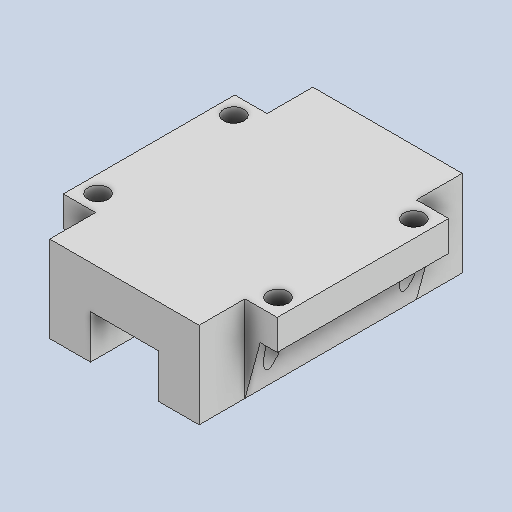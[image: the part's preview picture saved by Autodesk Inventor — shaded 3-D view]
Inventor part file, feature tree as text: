
AUTODESK INVENTOR PART (.ipt)
format: ipt  version: 2023 (Build 270158000, 158)  size: 184,832 bytes
history: native  units: mm
features: extrude x3, sketch x3
ambient origin geometry x8: Origin, YZ Plane, XZ Plane, XY Plane, X Axis, Y Axis, Z Axis, Center Point
bodies: Solid1 (feature_tree)
feature tree (6):
  extrude  "Extrusion1"  Depth=25.4mm
  extrude  "Extrusion2"  Depth=8.9mm
  extrude  "Extrusion3"  Depth=12.0mm
  sketch  "Sketch1"  dims[d0=63.0mm d1=25.4mm]
  sketch  "Sketch2"  dims[d4=21.5mm d5=8.9mm]
  sketch  "Sketch3"  dims[d6=12.9mm d7=12.0mm d8=5.0mm d9=50.5mm d10=0.0mm d11=13.5mm d12=64.0mm d13=0.0mm d14=0.0mm d15=6.0mm d16=40.0mm d17=53.0mm d18=34.5mm d19=0.0mm]
